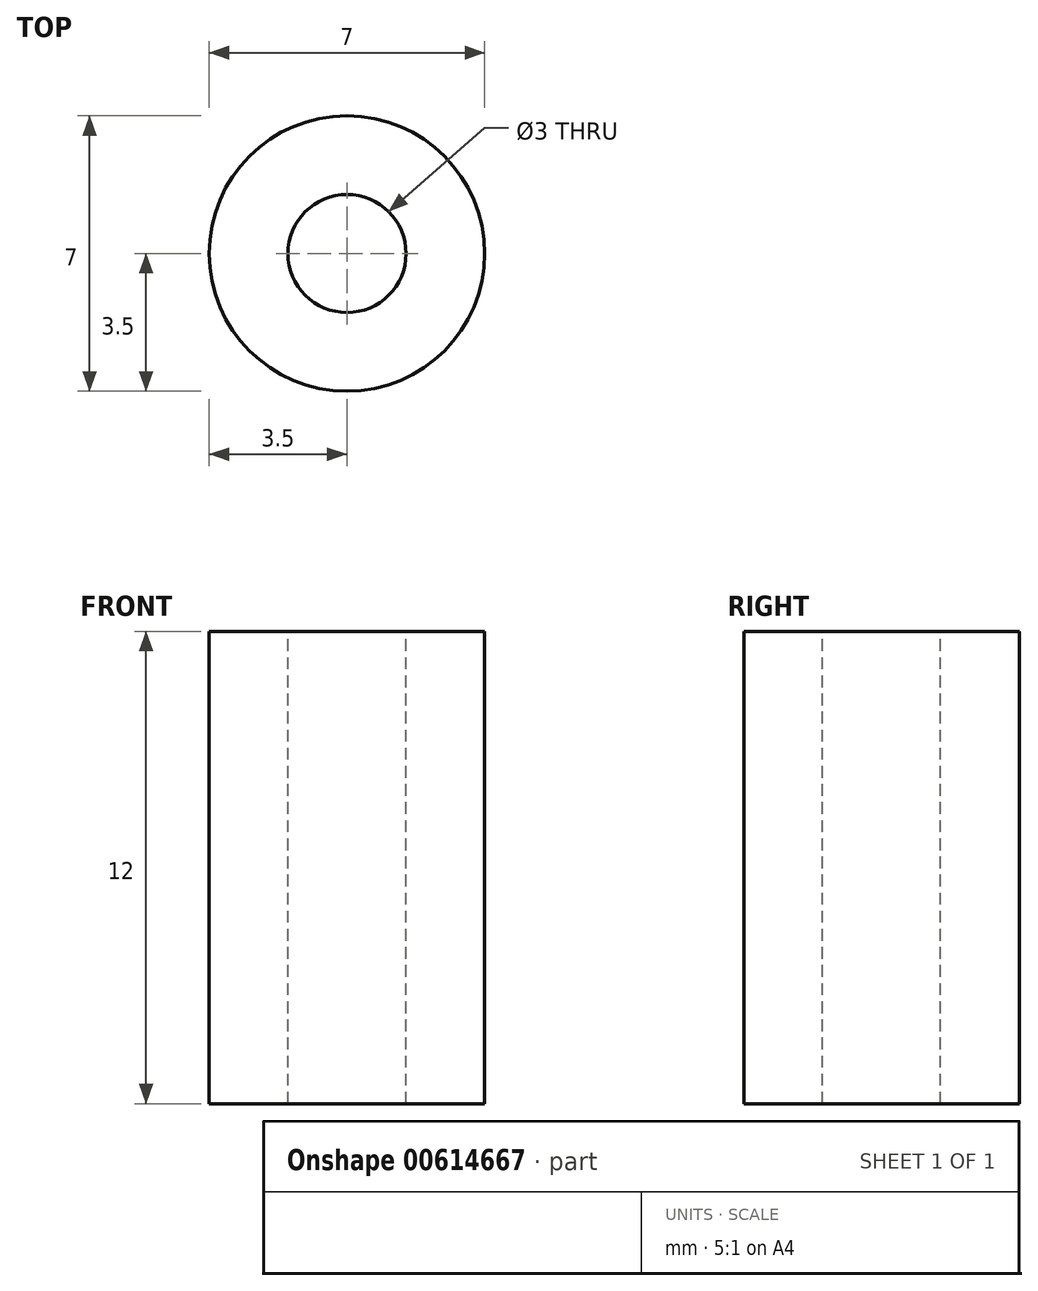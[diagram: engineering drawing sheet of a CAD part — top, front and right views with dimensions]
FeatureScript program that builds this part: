
annotation { "Feature Type Name" : "Feature", "Feature Type Description" : "" }
export const myFeature = defineFeature(function(context is Context, id is Id, definition is map)
    precondition{}
    {
        {
            var Q0;
            Q0=qCreatedBy(makeId("Top.planeOp"),FACE);
            var sketch = newSketch(context, id + "F0", { "sketchPlane" : qUnion([Q0])});
            skCircle(sketch, "E0", {"center": v(0, 0) * mm, "radius": 3.5 * mm});
            skSolve(sketch);
        }
        {
            var Q0;
            Q0 = qSketchRegion(id + "F0", true);
            extrude(context, id + "F1", {"entities" : qUnion([Q0]), "oppositeDirection" : true, "depth" : 12 * mm, "offsetDistance" : 25 * mm});
        }
        {
            var Q0;
            Q0=makeQuery(id+"F1.opExtrude","CAP_FACE",FACE,{"disambiguationData":[OSD([sQuery(id+"F0.wireOp",EDGE,"E0")])],"isStart":true});
            var sketch = newSketch(context, id + "F2", { "sketchPlane" : qUnion([Q0])});
            skCircle(sketch, "E1", {"center": v(0, 0) * mm, "radius": 1.5 * mm});
            skSolve(sketch);
        }
        {
            var Q0;
            Q0=makeQuery(id+"F2.imprint","IMPRINT",FACE,{"disambiguationData":[TD([[makeQuery(id+"F2.imprint","IMPRINT",EDGE,{"derivedFrom":sQuery(id+"F2.wireOp",EDGE,"E1")}),1.0]])]});
            extrude(context, id + "F3", {"entities" : qUnion([Q0]), "operationType" : NewBodyOperationType.REMOVE, "endBound" : BoundingType.THROUGH_ALL, "oppositeDirection" : true, "depth" : 25 * mm, "offsetDistance" : 25 * mm});
        }
    });
